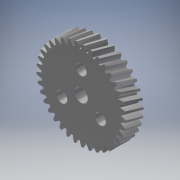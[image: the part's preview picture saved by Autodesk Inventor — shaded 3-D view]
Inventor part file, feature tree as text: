
AUTODESK INVENTOR PART (.ipt)
format: ipt  version: 2019 (Build 230136000, 136)  size: 613,376 bytes
history: native  units: mm (DEFAULTED — no unit token found)
features: sketch x4, plane x3, other x3, extrude x2, hole x1
ambient origin geometry x8: Origin, YZ Plane, XZ Plane, XY Plane, X Axis, Y Axis, Z Axis, Center Point
bodies: Solid1 (feature_tree)
feature tree (13):
  extrude  "Extrusion1"  Depth=10.0mm TaperAngle=0.0deg
  plane  "Work Plane2"
  plane  "Work Plane8"
  plane  "Work Plane9"
  other  "Spur Gear"
  extrude  "Extrusion2"  Depth=10.0mm TaperAngle=0.0deg
  hole  "Hole1"  [1 undecoded]
  sketch  "Sketch1"  dims[d0=50.240958mm d1=10.0mm d2=0.0mm]
  sketch  "Sketch2"  dims[d3=47.741935mm d4=10.0mm d5=0.0mm]
  other  "Srf1"
  sketch  "Sketch3"  dims[d16=40.0mm d17=0.0mm d34=0.849079mm]
  sketch  "Sketch4"  dims[d39=0.0mm d41=0.0mm d43=40.0mm d46=40.0mm d47=0.0mm d48=0.0mm d49=7.5mm d50=10.0mm d51=0.0mm d52=25.0mm d53=30.0mm d55=360.0deg d57=4.1mm d58=6.0mm d59=6.2mm d60=5.0mm d61=90.0deg d62=8.0mm d63=90.0deg]
  other  "Pitch Diameter"
note: 1 required parameter value undecoded (feature->parameter linkage not recoverable at this tier; creation-order binding heuristic only, values carry confidence <= 0.55)
